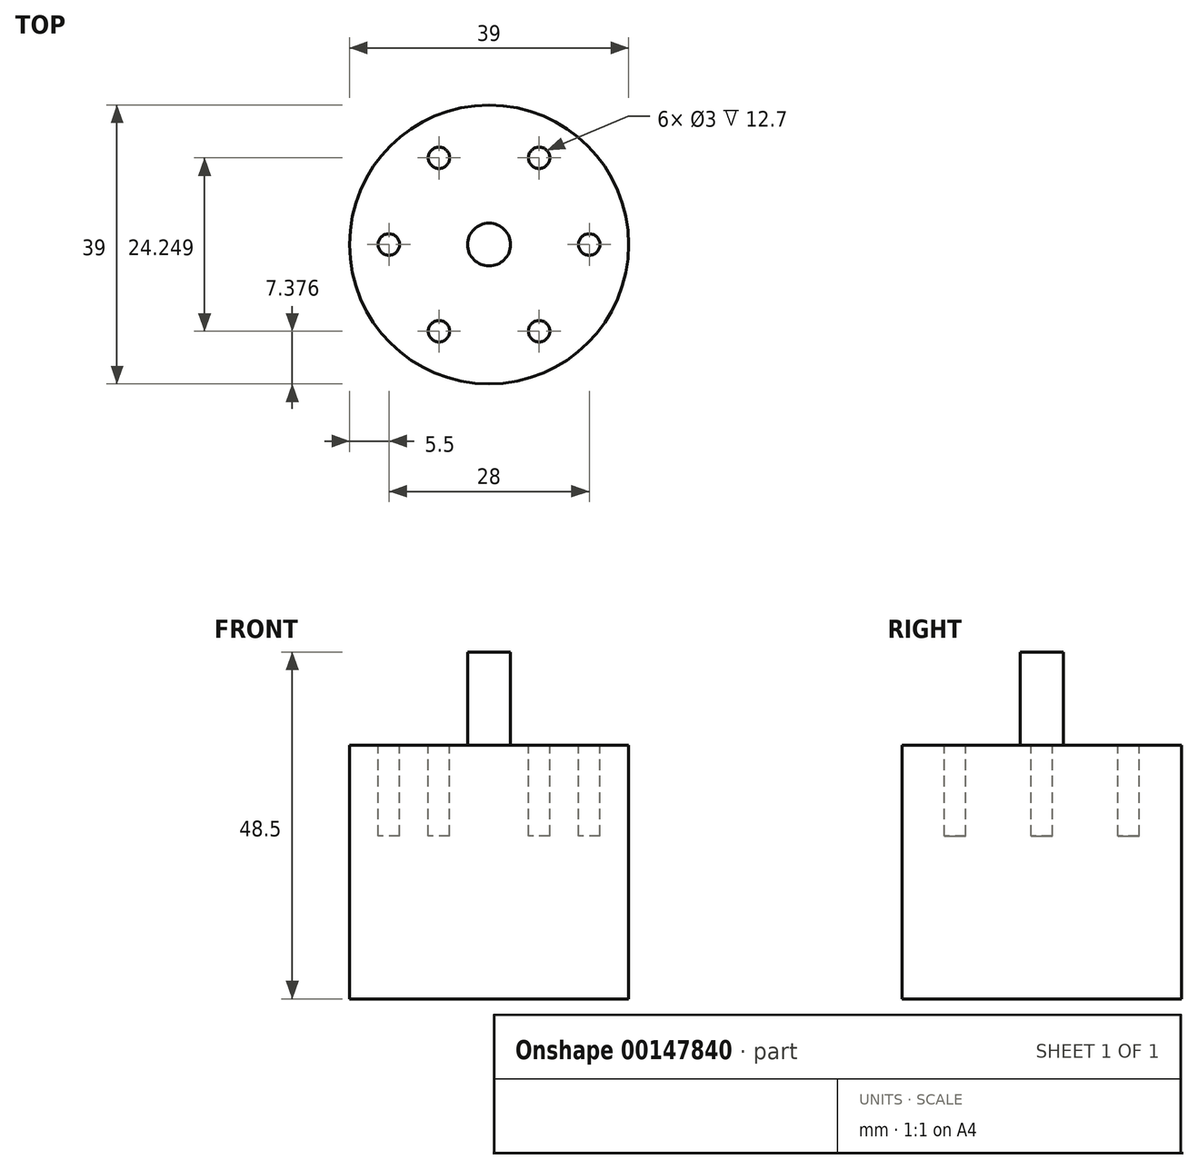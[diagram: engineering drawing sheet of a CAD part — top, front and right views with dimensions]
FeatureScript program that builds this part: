
annotation { "Feature Type Name" : "Feature", "Feature Type Description" : "" }
export const myFeature = defineFeature(function(context is Context, id is Id, definition is map)
    precondition{}
    {
        {
            var Q0;
            Q0=qCreatedBy(makeId("Top.planeOp"),FACE);
            var sketch = newSketch(context, id + "F0", { "sketchPlane" : qUnion([Q0])});
            skCircle(sketch, "E0", {"center": v(0, 0) * mm, "radius": 19.5 * mm});
            skSolve(sketch);
        }
        {
            var Q0;
            Q0=qSketchRegion(id+"F0",true);
            extrude(context, id + "F1", {"entities" : qUnion([Q0]), "depth" : 35.5 * mm});
        }
        {
            var Q0;
            Q0=makeQuery(id+"F1.opExtrude","CAP_FACE",FACE,{"disambiguationData":[OSD([sQuery(id+"F0.wireOp",EDGE,"E0")])],"isStart":false});
            var sketch = newSketch(context, id + "F2", { "sketchPlane" : qUnion([Q0])});
            skCircle(sketch, "E1", {"center": v(0, 0) * mm, "radius": 3 * mm});
            skSolve(sketch);
        }
        {
            var Q0;
            Q0=qSketchRegion(id+"F2",true);
            extrude(context, id + "F3", {"entities" : qUnion([Q0]), "operationType" : NewBodyOperationType.ADD, "depth" : 13 * mm});
        }
        {
            var Q0;
            Q0=makeQuery(id+"F1.opExtrude","CAP_FACE",FACE,{"disambiguationData":[OSD([sQuery(id+"F0.wireOp",EDGE,"E0")])],"isStart":false});
            var sketch = newSketch(context, id + "F4", { "sketchPlane" : qUnion([Q0])});
            skLineSegment(sketch, "E2", {"start": v(0, 0) * mm, "end": v(0, 12.12) * mm, "construction": true});
            skLineSegment(sketch, "E3", {"start": v(0, 0) * mm, "end": v(10.5, -6.06) * mm, "construction": true});
            skLineSegment(sketch, "E4", {"start": v(0, 0) * mm, "end": v(-10.5, -6.06) * mm, "construction": true});
            skLineSegment(sketch, "E5", {"start": v(-10.5, -6.06) * mm, "end": v(0, 12.12) * mm, "construction": true});
            skLineSegment(sketch, "E6", {"start": v(0, 12.12) * mm, "end": v(10.5, -6.06) * mm, "construction": true});
            skLineSegment(sketch, "E7", {"start": v(10.5, -6.06) * mm, "end": v(-10.5, -6.06) * mm, "construction": true});
            skLineSegment(sketch, "E8", {"start": v(-14, 0) * mm, "end": v(-7, -12.12) * mm, "construction": true});
            skLineSegment(sketch, "E9", {"start": v(-7, 12.12) * mm, "end": v(7, 12.12) * mm, "construction": true});
            skLineSegment(sketch, "E10", {"start": v(7, -12.12) * mm, "end": v(14, 0) * mm, "construction": true});
            skLineSegment(sketch, "E11", {"start": v(7, -12.12) * mm, "end": v(0, 0) * mm, "construction": true});
            skCircle(sketch, "E12", {"center": v(-7, -12.12) * mm, "radius": 1.5 * mm});
            skCircle(sketch, "E13", {"center": v(-14, 0) * mm, "radius": 1.5 * mm});
            skCircle(sketch, "E14", {"center": v(-7, 12.12) * mm, "radius": 1.5 * mm});
            skCircle(sketch, "E15", {"center": v(7, 12.12) * mm, "radius": 1.5 * mm});
            skCircle(sketch, "E16", {"center": v(14, 0) * mm, "radius": 1.5 * mm});
            skCircle(sketch, "E17", {"center": v(7, -12.12) * mm, "radius": 1.5 * mm});
            skSolve(sketch);
        }
        {
            var Q0;
            Q0=qSketchRegion(id+"F4",true);
            extrude(context, id + "F5", {"entities" : qUnion([Q0]), "operationType" : NewBodyOperationType.REMOVE, "oppositeDirection" : true, "depth" : 12.7 * mm});
        }
    });
